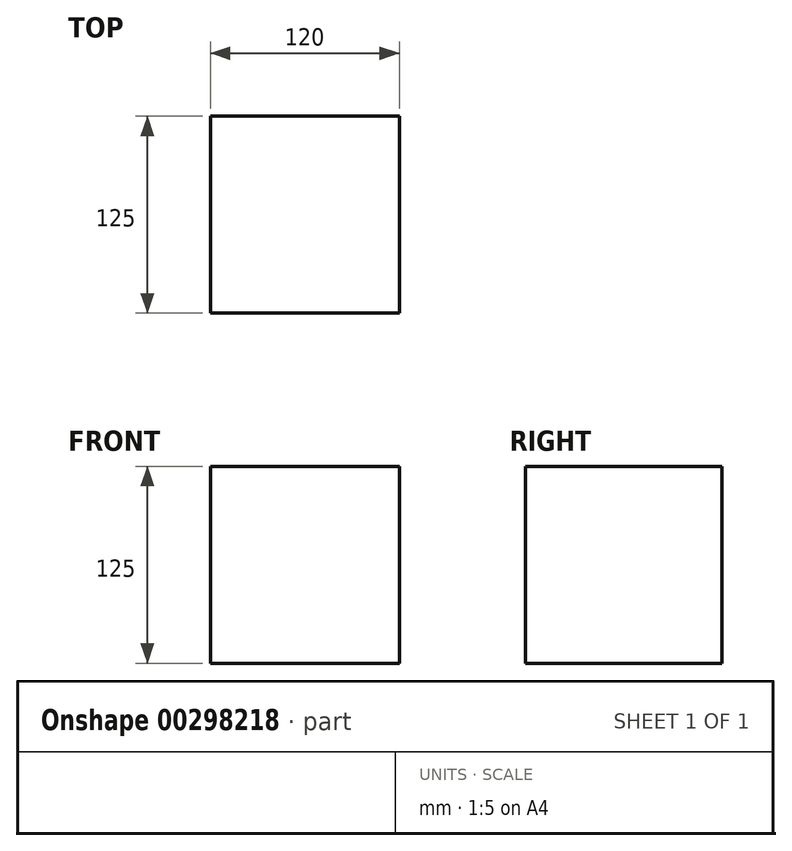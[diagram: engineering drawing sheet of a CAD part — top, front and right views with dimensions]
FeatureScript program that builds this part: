
annotation { "Feature Type Name" : "Feature", "Feature Type Description" : "" }
export const myFeature = defineFeature(function(context is Context, id is Id, definition is map)
    precondition{}
    {
        {
            var Q0;
            Q0=qCreatedBy(makeId("Top.planeOp"),FACE);
            cPlane(context, id + "F0", {"entities" : qUnion([Q0]), "cplaneType" : CPlaneType.OFFSET, "offset" : 0 * mm, "width" : 150 * mm, "height" : 150 * mm});
        }
        {
            var Q0;
            Q0=qCreatedBy(id+"F0.planeOp",FACE);
            var sketch = newSketch(context, id + "F1", { "sketchPlane" : qUnion([Q0])});
            skLineSegment(sketch, "E0.bottom", {"start": v(-60, -62.5) * mm, "end": v(60, -62.5) * mm});
            skLineSegment(sketch, "E0.top", {"start": v(-60, 62.5) * mm, "end": v(60, 62.5) * mm});
            skLineSegment(sketch, "E0.left", {"start": v(-60, -62.5) * mm, "end": v(-60, 62.5) * mm});
            skLineSegment(sketch, "E0.right", {"start": v(60, -62.5) * mm, "end": v(60, 62.5) * mm});
            skLineSegment(sketch, "E1", {"start": v(-60, 62.5) * mm, "end": v(60, -62.5) * mm, "construction": true});
            skLineSegment(sketch, "E2", {"start": v(-60, -62.5) * mm, "end": v(60, 62.5) * mm, "construction": true});
            skPoint(sketch, "E3", {"position": v(0, 0) * mm});
            skSolve(sketch);
        }
        {
            var Q0;
            Q0 = qSketchRegion(id + "F1", true);
            extrude(context, id + "F2", {"entities" : qUnion([Q0]), "depth" : 125 * mm});
        }
    });
